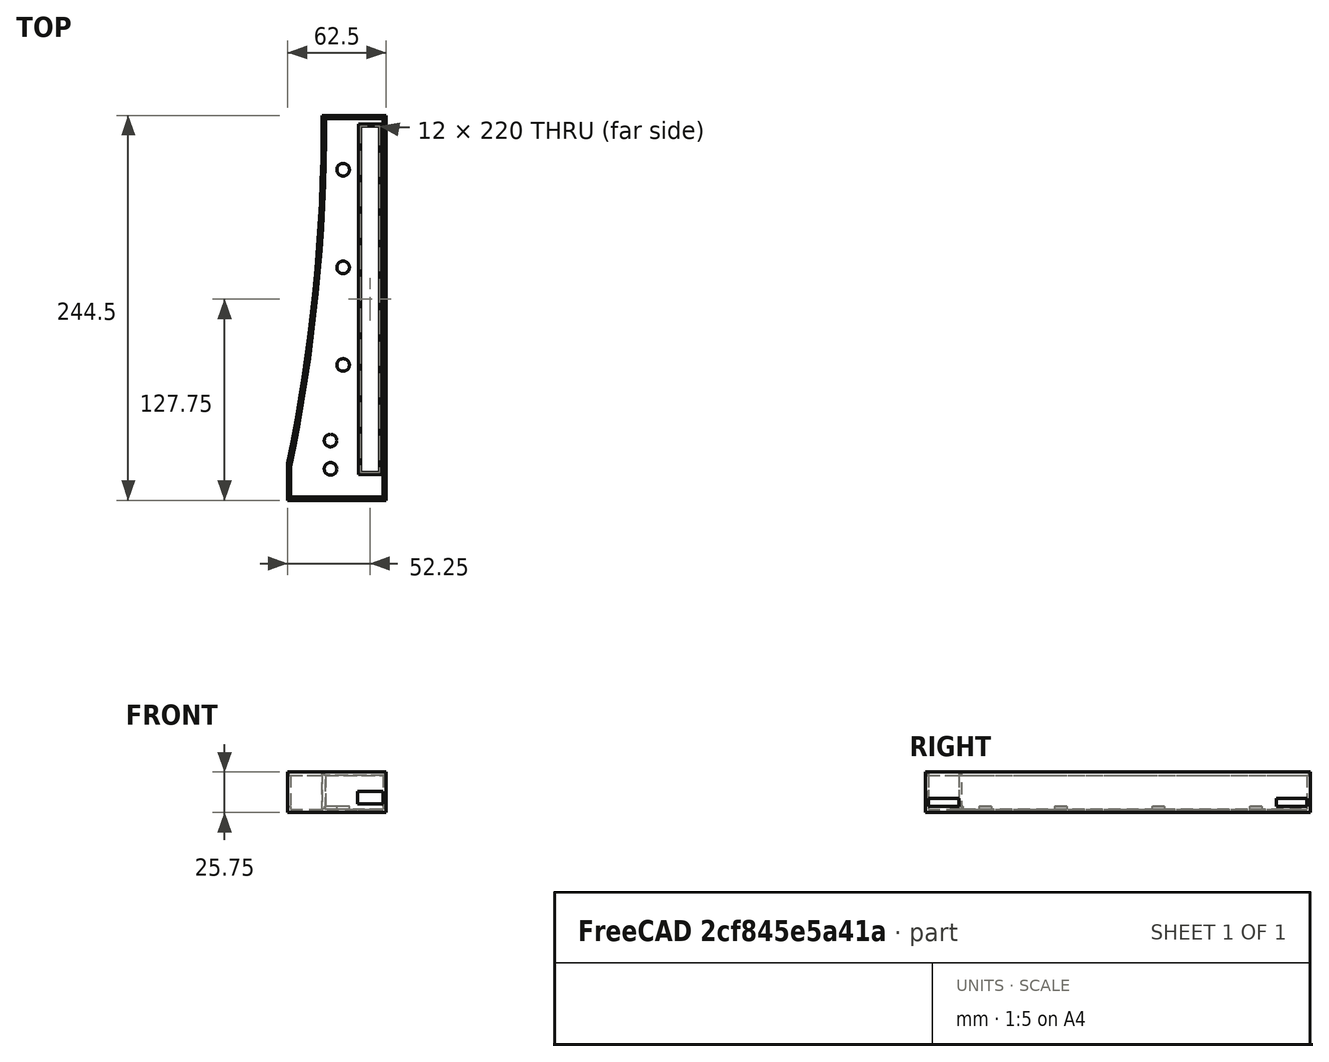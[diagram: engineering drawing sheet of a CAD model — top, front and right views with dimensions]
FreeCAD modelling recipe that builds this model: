
FCSTD DOCUMENT  (FreeCAD 0.19R)
Label: case-bottom
License: All rights reserved
LicenseURL: http://en.wikipedia.org/wiki/All_rights_reserved
objects: Sketcher::SketchObject×9, PartDesign::Pocket×7, PartDesign::Pad×2, Image::ImagePlane×1, PartDesign::Body×1, Mesh::Feature×1
note: 28 computed .brp shape members not serialized (recipe doc carries the construction recipe); baked Part::Feature solids carry a one-line shape summary decoded from their .brp

FEATURE [Sketcher::SketchObject] Sketch
  FullyConstrained = true
  MapMode = 5
  Support = -> [XY_Plane]
  sketch-geometry (5):
    g0: LineSegment StartX=70.75 StartY=0 StartZ=0 EndX=70.75 EndY=244.5 EndZ=0
    g1: LineSegment StartX=70.75 StartY=244.5 StartZ=0 EndX=30.25 EndY=244.5 EndZ=0
    g2: LineSegment StartX=70.75 StartY=0 StartZ=0 EndX=8.25 EndY=0 EndZ=0
    g3: LineSegment StartX=8.25 StartY=0 StartZ=0 EndX=8.25 EndY=23.5 EndZ=0
    g4: ArcOfCircle CenterX=-1044.74 CenterY=239.918 CenterZ=0 NormalX=0 NormalY=0 NormalZ=1 AngleXU=0 Radius=1075 StartAngle=6.08048 EndAngle=6.28745
  constraints (16):
    c: PointOnObject(g0,g-1)
    c: Vertical(g0)
    c: Coincident(g1,g0)
    c: Horizontal(g1)
    c: Coincident(g2,g0)
    c: PointOnObject(g2,g-1)
    c: Coincident(g3,g2)
    c: Vertical(g3)
    c: Coincident(g4,g3)
    c: Coincident(g4,g1)
    c: DistanceX(g-1,g2) = 8.25
    c: DistanceX(g2,g2) = 62.5
    c: DistanceY(g0,g0) = 244.5
    c: DistanceX(g1,g1) = 40.5
    c: DistanceY(g3,g3) = 23.5
    c: Diameter(g4) = 2150
FEATURE [PartDesign::Pad] Pad
  Direction = (1,1,1)
  Length = 25.75
  Length2 = 100
  Profile = -> Sketch
  Type = 0
FEATURE [Sketcher::SketchObject] Sketch001
  FullyConstrained = true
  MapMode = 5
  Placement = pos=(0,0,25.75) rot=(0,0,1;0rad)
  Support = -> [Pad]
  sketch-geometry (5):
    g0: LineSegment StartX=10.25 StartY=2 StartZ=0 EndX=68.75 EndY=2 EndZ=0
    g1: LineSegment StartX=68.75 StartY=2 StartZ=0 EndX=68.75 EndY=242.5 EndZ=0
    g2: LineSegment StartX=68.75 StartY=242.5 StartZ=0 EndX=32.25 EndY=242.5 EndZ=0
    g3: ArcOfCircle CenterX=-1042.74 CenterY=237.918 CenterZ=0 NormalX=0 NormalY=0 NormalZ=1 AngleXU=0 Radius=1075 StartAngle=6.08048 EndAngle=6.28745
    g4: LineSegment StartX=10.25 StartY=2 StartZ=0 EndX=10.25 EndY=21.5 EndZ=0
  constraints (16):
    c: Horizontal(g0)
    c: Coincident(g1,g0)
    c: Vertical(g1)
    c: DistanceX(g-1,g0) = 10.25
    c: DistanceY(g-1,g0) = 2
    c: DistanceX(g0,g0) = 58.5
    c: Coincident(g2,g1)
    c: Horizontal(g2)
    c: Coincident(g3,g2)
    c: Coincident(g4,g0)
    c: Vertical(g4)
    c: Coincident(g3,g4)
    c: DistanceY(g1,g1) = 240.5
    c: DistanceX(g2,g2) = 36.5
    c: DistanceY(g4,g4) = 19.5
    c: Diameter(g3) = 2150
FEATURE [PartDesign::Pocket] Pocket
  BaseFeature = -> Pad
  Length = 23.75
  Length2 = 100
  Profile = -> Sketch001
  Type = 0
FEATURE [Image::ImagePlane] ImagePlane
  Placement = pos=(39.5,122.25,0) rot=(0,0,1;0rad)
  XSize = 74
  YSize = 240
FEATURE [Sketcher::SketchObject] Sketch002
  FullyConstrained = true
  MapMode = 5
  Placement = pos=(0,0,25.75) rot=(0,0,1;0rad)
  Support = -> [Pocket]
  sketch-geometry (4):
    g0: LineSegment StartX=8.25 StartY=2 StartZ=0 EndX=10.25 EndY=2 EndZ=0
    g1: LineSegment StartX=10.25 StartY=2 StartZ=0 EndX=10.25 EndY=21.5 EndZ=0
    g2: LineSegment StartX=10.25 StartY=21.5 StartZ=0 EndX=8.25 EndY=21.5 EndZ=0
    g3: LineSegment StartX=8.25 StartY=21.5 StartZ=0 EndX=8.25 EndY=2 EndZ=0
  constraints (12):
    c: Coincident(g0,g1)
    c: Coincident(g1,g2)
    c: Coincident(g2,g3)
    c: Coincident(g3,g0)
    c: Horizontal(g0)
    c: Horizontal(g2)
    c: Vertical(g1)
    c: Vertical(g3)
    c: DistanceX(g-1,g0) = 8.25
    c: DistanceY(g-1,g0) = 2
    c: DistanceX(g2,g2) = 2
    c: DistanceY(g1,g1) = 19.5
FEATURE [PartDesign::Pocket] Pocket001
  BaseFeature = -> Pocket
  Length = 21.75
  Length2 = 100
  Profile = -> Sketch002
  Type = 0
FEATURE [Sketcher::SketchObject] Sketch003
  FullyConstrained = true
  MapMode = 5
  Placement = pos=(70.75,0,0) rot=(0.57735,0.57735,0.57735;2.0944rad)
  Support = -> [Pocket001]
  sketch-geometry (8):
    g0: LineSegment StartX=2 StartY=4 StartZ=0 EndX=21.5 EndY=4 EndZ=0
    g1: LineSegment StartX=21.5 StartY=4 StartZ=0 EndX=21.5 EndY=9 EndZ=0
    g2: LineSegment StartX=21.5 StartY=9 StartZ=0 EndX=2 EndY=9 EndZ=0
    g3: LineSegment StartX=2 StartY=9 StartZ=0 EndX=2 EndY=4 EndZ=0
    g4: LineSegment StartX=242.5 StartY=4 StartZ=0 EndX=223 EndY=4 EndZ=0
    g5: LineSegment StartX=223 StartY=4 StartZ=0 EndX=223 EndY=9 EndZ=0
    g6: LineSegment StartX=223 StartY=9 StartZ=0 EndX=242.5 EndY=9 EndZ=0
    g7: LineSegment StartX=242.5 StartY=9 StartZ=0 EndX=242.5 EndY=4 EndZ=0
  constraints (24):
    c: Coincident(g0,g1)
    c: Coincident(g1,g2)
    c: Coincident(g2,g3)
    c: Coincident(g3,g0)
    c: Horizontal(g0)
    c: Horizontal(g2)
    c: Vertical(g1)
    c: Vertical(g3)
    c: Coincident(g4,g5)
    c: Coincident(g5,g6)
    c: Coincident(g6,g7)
    c: Coincident(g7,g4)
    c: Horizontal(g4)
    c: Horizontal(g6)
    c: Vertical(g5)
    c: Vertical(g7)
    c: DistanceX(g-1,g0) = 2
    c: DistanceY(g-1,g0) = 4
    c: DistanceX(g2,g2) = 19.5
    c: DistanceY(g1,g1) = 5
    c: DistanceY(g-1,g4) = 4
    c: DistanceX(g-1,g4) = 223
    c: DistanceX(g6,g6) = 19.5
    c: DistanceY(g7,g7) = 5
FEATURE [PartDesign::Pocket] Pocket002
  BaseFeature = -> Pocket001
  Length = 5
  Length2 = 100
  Profile = -> Sketch003
  Type = 2
FEATURE [Sketcher::SketchObject] Sketch004
  FullyConstrained = true
  MapMode = 5
  Placement = pos=(0,0,0) rot=(1,0,0;1.5708rad)
  Support = -> [Pocket002]
  sketch-geometry (4):
    g0: LineSegment StartX=68.75 StartY=5.5 StartZ=0 EndX=52.75 EndY=5.5 EndZ=0
    g1: LineSegment StartX=52.75 StartY=5.5 StartZ=0 EndX=52.75 EndY=13.5 EndZ=0
    g2: LineSegment StartX=52.75 StartY=13.5 StartZ=0 EndX=68.75 EndY=13.5 EndZ=0
    g3: LineSegment StartX=68.75 StartY=13.5 StartZ=0 EndX=68.75 EndY=5.5 EndZ=0
  constraints (12):
    c: Coincident(g0,g1)
    c: Coincident(g1,g2)
    c: Coincident(g2,g3)
    c: Coincident(g3,g0)
    c: Horizontal(g0)
    c: Horizontal(g2)
    c: Vertical(g1)
    c: Vertical(g3)
    c: DistanceY(g-1,g0) = 5.5
    c: DistanceX(g-1,g0) = 52.75
    c: DistanceY(g3,g3) = 8
    c: DistanceX(g2,g2) = 16
FEATURE [PartDesign::Pocket] Pocket003
  BaseFeature = -> Pocket002
  Length = 5
  Length2 = 100
  Profile = -> Sketch004
  Type = 2
FEATURE [Sketcher::SketchObject] Sketch005
  FullyConstrained = true
  MapMode = 5
  Placement = pos=(0,0,4) rot=(0,0,1;0rad)
  Support = -> [Pocket003]
  sketch-geometry (4):
    g0: LineSegment StartX=66.5 StartY=17.75 StartZ=0 EndX=54.5 EndY=17.75 EndZ=0
    g1: LineSegment StartX=54.5 StartY=17.75 StartZ=0 EndX=54.5 EndY=237.75 EndZ=0
    g2: LineSegment StartX=54.5 StartY=237.75 StartZ=0 EndX=66.5 EndY=237.75 EndZ=0
    g3: LineSegment StartX=66.5 StartY=237.75 StartZ=0 EndX=66.5 EndY=17.75 EndZ=0
  constraints (12):
    c: Coincident(g0,g1)
    c: Coincident(g1,g2)
    c: Coincident(g2,g3)
    c: Coincident(g3,g0)
    c: Horizontal(g0)
    c: Horizontal(g2)
    c: Vertical(g1)
    c: Vertical(g3)
    c: DistanceX(g2,g2) = 12
    c: DistanceY(g3,g3) = 220
    c: DistanceX(g-1,g0) = 54.5
    c: DistanceY(g-1,g0) = 17.75
FEATURE [PartDesign::Pocket] Pocket004
  BaseFeature = -> Pocket003
  Length = 5
  Length2 = 100
  Profile = -> Sketch005
  Type = 1
FEATURE [Sketcher::SketchObject] Sketch006
  FullyConstrained = true
  MapMode = 5
  Placement = pos=(0,0,2) rot=(0,0,1;0rad)
  Support = -> [Pocket004]
  sketch-geometry (4):
    g0: LineSegment StartX=67.75 StartY=16.5 StartZ=0 EndX=53.25 EndY=16.5 EndZ=0
    g1: LineSegment StartX=53.25 StartY=16.5 StartZ=0 EndX=53.25 EndY=239 EndZ=0
    g2: LineSegment StartX=53.25 StartY=239 StartZ=0 EndX=67.75 EndY=239 EndZ=0
    g3: LineSegment StartX=67.75 StartY=239 StartZ=0 EndX=67.75 EndY=16.5 EndZ=0
  constraints (12):
    c: Coincident(g0,g1)
    c: Coincident(g1,g2)
    c: Coincident(g2,g3)
    c: Coincident(g3,g0)
    c: Horizontal(g0)
    c: Horizontal(g2)
    c: Vertical(g1)
    c: Vertical(g3)
    c: DistanceX(g2,g2) = 14.5
    c: DistanceY(g3,g3) = 222.5
    c: DistanceX(g-1,g0) = 53.25
    c: DistanceY(g-1,g0) = 16.5
FEATURE [PartDesign::Pocket] Pocket005
  BaseFeature = -> Pocket004
  Length = 1.25
  Length2 = 100
  Profile = -> Sketch006
  Type = 0
FEATURE [Sketcher::SketchObject] Sketch007
  FullyConstrained = true
  MapMode = 5
  Placement = pos=(0,0,25.75) rot=(0,0,1;0rad)
  Support = -> [Pocket005]
  sketch-geometry (5):
    g0: LineSegment StartX=9.25 StartY=1 StartZ=0 EndX=9.25 EndY=22.5 EndZ=0
    g1: LineSegment StartX=9.25 StartY=1 StartZ=0 EndX=69.75 EndY=1 EndZ=0
    g2: LineSegment StartX=69.75 StartY=1 StartZ=0 EndX=69.75 EndY=243.5 EndZ=0
    g3: LineSegment StartX=69.75 StartY=243.5 StartZ=0 EndX=31.25 EndY=243.5 EndZ=0
    g4: ArcOfCircle CenterX=-1043.74 CenterY=238.918 CenterZ=0 NormalX=0 NormalY=0 NormalZ=1 AngleXU=0 Radius=1075 StartAngle=6.08048 EndAngle=6.28745
  constraints (16):
    c: Vertical(g0)
    c: Coincident(g1,g0)
    c: Horizontal(g1)
    c: Coincident(g2,g1)
    c: Vertical(g2)
    c: Coincident(g3,g2)
    c: Horizontal(g3)
    c: Coincident(g4,g0)
    c: Coincident(g4,g3)
    c: DistanceY(g-1,g0) = 1
    c: DistanceX(g-1,g0) = 9.25
    c: DistanceX(g1,g1) = 60.5
    c: DistanceY(g0,g0) = 21.5
    c: DistanceY(g2,g2) = 242.5
    c: DistanceX(g3,g3) = 38.5
    c: Diameter(g4) = 2150
FEATURE [PartDesign::Pocket] Pocket006
  BaseFeature = -> Pocket005
  Length = 2.25
  Length2 = 100
  Profile = -> Sketch007
  Type = 0
FEATURE [Sketcher::SketchObject] Sketch008
  FullyConstrained = true
  MapMode = 5
  Placement = pos=(0,0,2) rot=(0,0,1;0rad)
  Support = -> [Pocket006]
  sketch-geometry (8):
    g0: Circle CenterX=35.5 CenterY=38 CenterZ=0 NormalX=0 NormalY=0 NormalZ=1 AngleXU=0 Radius=4
    g1: Circle CenterX=43.5 CenterY=86 CenterZ=0 NormalX=0 NormalY=0 NormalZ=1 AngleXU=0 Radius=4
    g2: Circle CenterX=43.5 CenterY=148 CenterZ=0 NormalX=0 NormalY=0 NormalZ=1 AngleXU=0 Radius=4
    g3: Circle CenterX=43.5 CenterY=210 CenterZ=0 NormalX=0 NormalY=0 NormalZ=1 AngleXU=0 Radius=4
    g4: LineSegment StartX=0 StartY=12 StartZ=0 EndX=43.5 EndY=12 EndZ=0
    g5: LineSegment StartX=35.5 StartY=12 StartZ=0 EndX=35.5 EndY=38 EndZ=0
    g6: LineSegment StartX=43.5 StartY=12 StartZ=0 EndX=43.5 EndY=210 EndZ=0
    g7: Circle CenterX=35.5 CenterY=20 CenterZ=0 NormalX=0 NormalY=0 NormalZ=1 AngleXU=0 Radius=4
  constraints (24):
    c: Equal(g1,g2)
    c: Equal(g2,g3)
    c: PointOnObject(g4,g-2)
    c: Horizontal(g4)
    c: PointOnObject(g5,g4)
    c: Coincident(g5,g0)
    c: Vertical(g5)
    c: Coincident(g6,g4)
    c: Coincident(g6,g3)
    c: Vertical(g6)
    c: PointOnObject(g2,g6)
    c: PointOnObject(g1,g6)
    c: DistanceX(g4,g4) = 43.5
    c: DistanceY(g-1,g4) = 12
    c: PointOnObject(g7,g5)
    c: DistanceY(g5,g7) = 8
    c: Equal(g7,g0)
    c: Diameter(g7) = 8
    c: DistanceY(g5,g5) = 26
    c: DistanceX(g4,g5) = 35.5
    c: DistanceY(g6,g6) = 198
    c: DistanceY(g4,g1) = 74
    c: DistanceY(g4,g2) = 136
    c: Equal(g1,g0)
FEATURE [PartDesign::Pad] Pad001
  BaseFeature = -> Pocket006
  Direction = (1,1,1)
  Length = 1.75
  Length2 = 100
  Profile = -> Sketch008
  Type = 0
FEATURE [PartDesign::Body] Body
  Group = -> [Sketch,Pad,Sketch001,Pocket,Sketch002,Pocket001,Sketch003,Pocket002,Sketch004,Pocket003,Sketch005,Pocket004,Sketch006,Pocket005,Sketch007,Pocket006,Sketch008,Pad001]
  Origin = -> Origin
  Tip = -> Pad001
FEATURE [Mesh::Feature] Mesh  label="Body (Meshed)"
